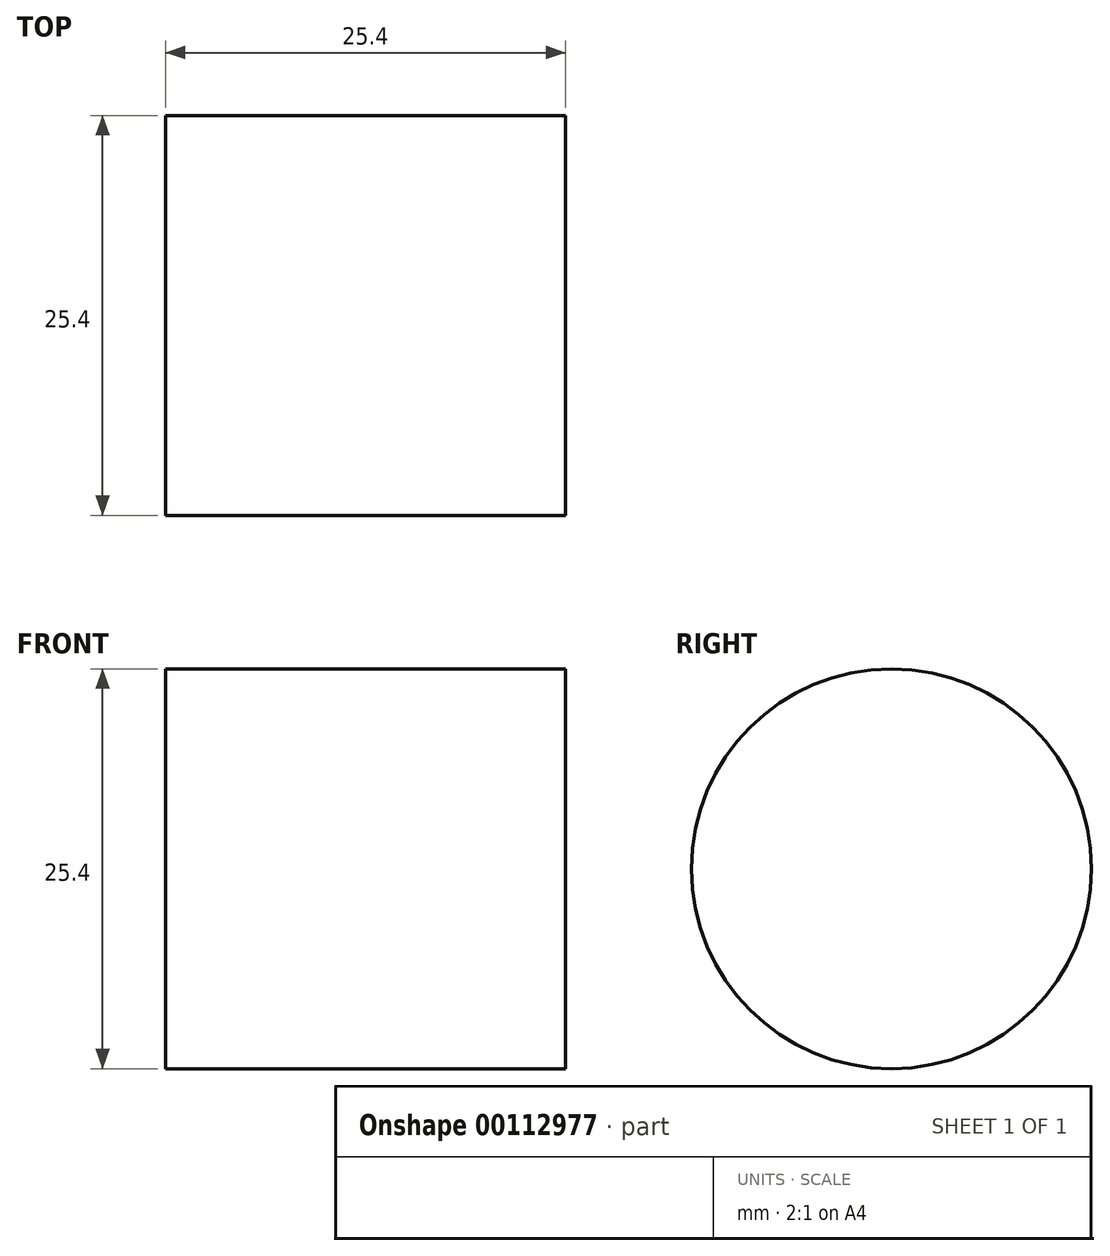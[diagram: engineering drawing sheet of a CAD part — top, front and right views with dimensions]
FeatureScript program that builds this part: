
annotation { "Feature Type Name" : "Feature", "Feature Type Description" : "" }
export const myFeature = defineFeature(function(context is Context, id is Id, definition is map)
    precondition{}
    {
        {
            var Q0;
            Q0=qCreatedBy(makeId("Right.planeOp"),FACE);
            var sketch = newSketch(context, id + "F0", { "sketchPlane" : qUnion([Q0])});
            skCircle(sketch, "E0", {"center": v(0, 0) * mm, "radius": 12.7 * mm});
            skSolve(sketch);
        }
        {
            var Q0;
            Q0=makeQuery(id+"F0.imprint","IMPRINT",FACE,{"disambiguationData":[TD([[makeQuery(id+"F0.imprint","IMPRINT",EDGE,{"derivedFrom":sQuery(id+"F0.wireOp",EDGE,"E0")}),1.0]])]});
            var Q1;
            Q1=sQuery(id+"F0.wireOp",EDGE,"E0");
            extrude(context, id + "F1", {"entities" : qUnion([Q0]), "surfaceEntities" : qUnion([Q1]), "depth" : 25.4 * mm});
        }
    });
